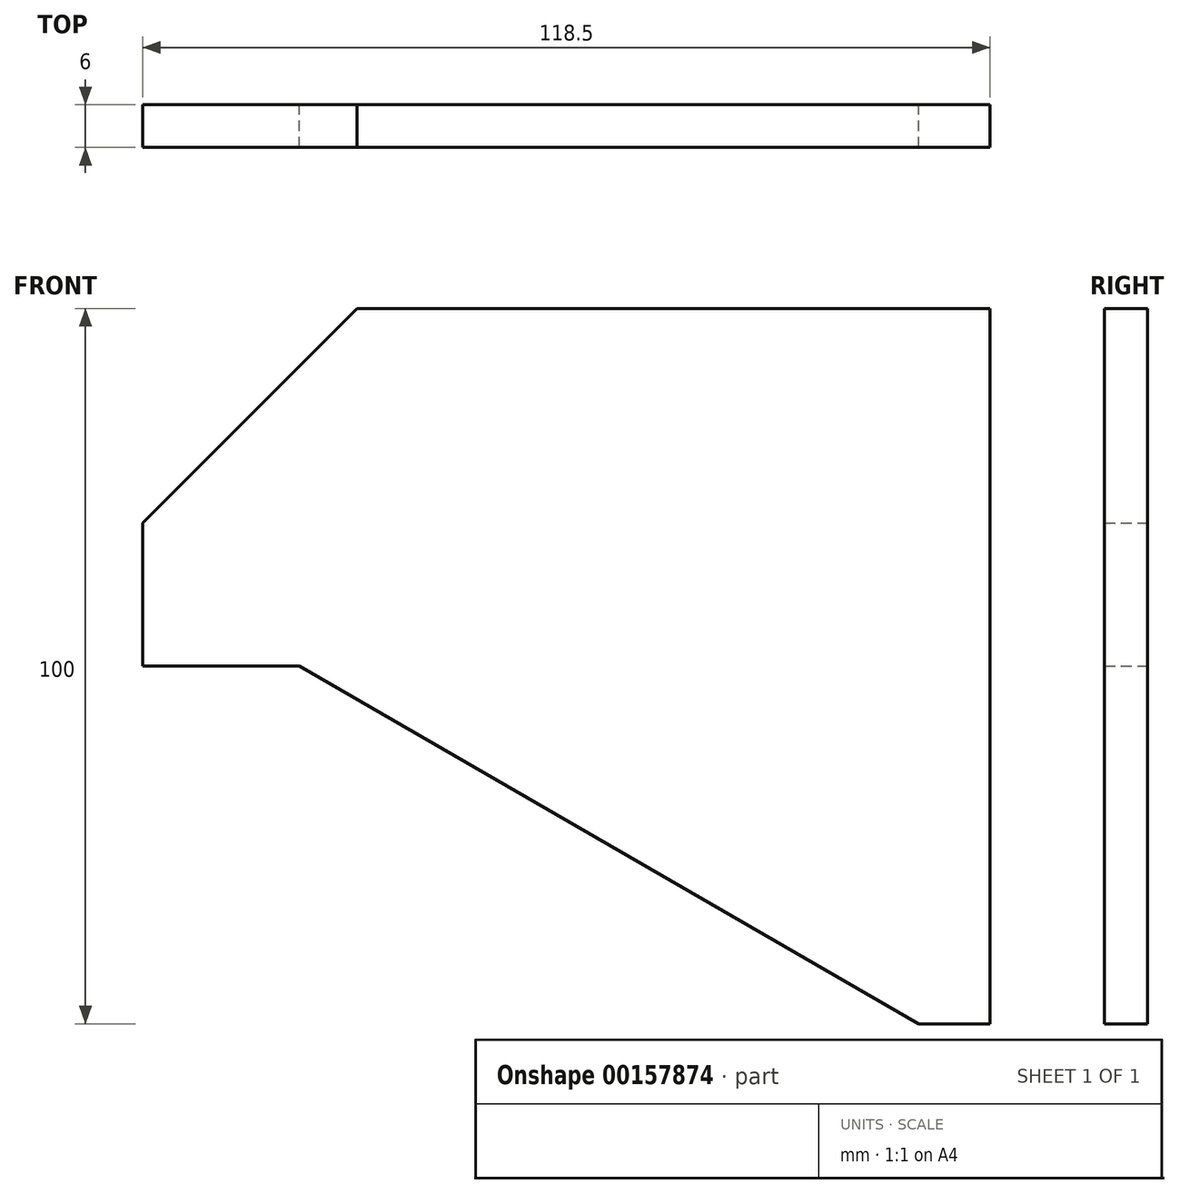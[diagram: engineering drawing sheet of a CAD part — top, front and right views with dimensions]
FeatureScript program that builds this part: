
annotation { "Feature Type Name" : "Feature", "Feature Type Description" : "" }
export const myFeature = defineFeature(function(context is Context, id is Id, definition is map)
    precondition{}
    {
        {
            var Q0;
            Q0=qCreatedBy(makeId("Front.planeOp"),FACE);
            var sketch = newSketch(context, id + "F0", { "sketchPlane" : qUnion([Q0])});
            skLineSegment(sketch, "E0.bottom", {"start": v(0, 50) * mm, "end": v(-118.5, 50) * mm});
            skPoint(sketch, "E1.start.orphan", {"position": v(0, 0) * mm});
            skLineSegment(sketch, "E2", {"start": v(-118.5, 50) * mm, "end": v(-118.5, 0) * mm});
            skLineSegment(sketch, "E3", {"start": v(0, 50) * mm, "end": v(0, -50) * mm});
            skLineSegment(sketch, "E4", {"start": v(0, -50) * mm, "end": v(-10, -50) * mm});
            skLineSegment(sketch, "E5", {"start": v(-10, -50) * mm, "end": v(-96.6, 0) * mm});
            skLineSegment(sketch, "E6.trimOffspring", {"start": v(-96.6, 0) * mm, "end": v(-118.5, 0) * mm});
            skLineSegment(sketch, "E7", {"start": v(50.6, 0) * mm, "end": v(-154.83, 0) * mm, "construction": true});
            skSolve(sketch);
        }
        {
            var Q0;
            Q0=makeQuery(id+"F0.imprint","IMPRINT",FACE,{"disambiguationData":[TD([[makeQuery(id+"F0.imprint","IMPRINT",EDGE,{"derivedFrom":sQuery(id+"F0.wireOp",EDGE,"E0.bottom")}),1.0]])]});
            extrude(context, id + "F1", {"entities" : qUnion([Q0]), "endBound" : BoundingType.SYMMETRIC, "depth" : 6 * mm});
        }
        {
            var Q0;
            Q0=makeQuery(id+"F1.opExtrude","SWEPT_EDGE",EDGE,{"disambiguationData":[OSD([sQuery(id+"F0.wireOp",EDGE,"E0.bottom"),sQuery(id+"F0.wireOp",EDGE,"E2")])]});
            chamfer(context, id + "F2", {"entities" : qUnion([Q0]), "width" : 30 * mm, "tangentPropagation" : true});
        }
    });
